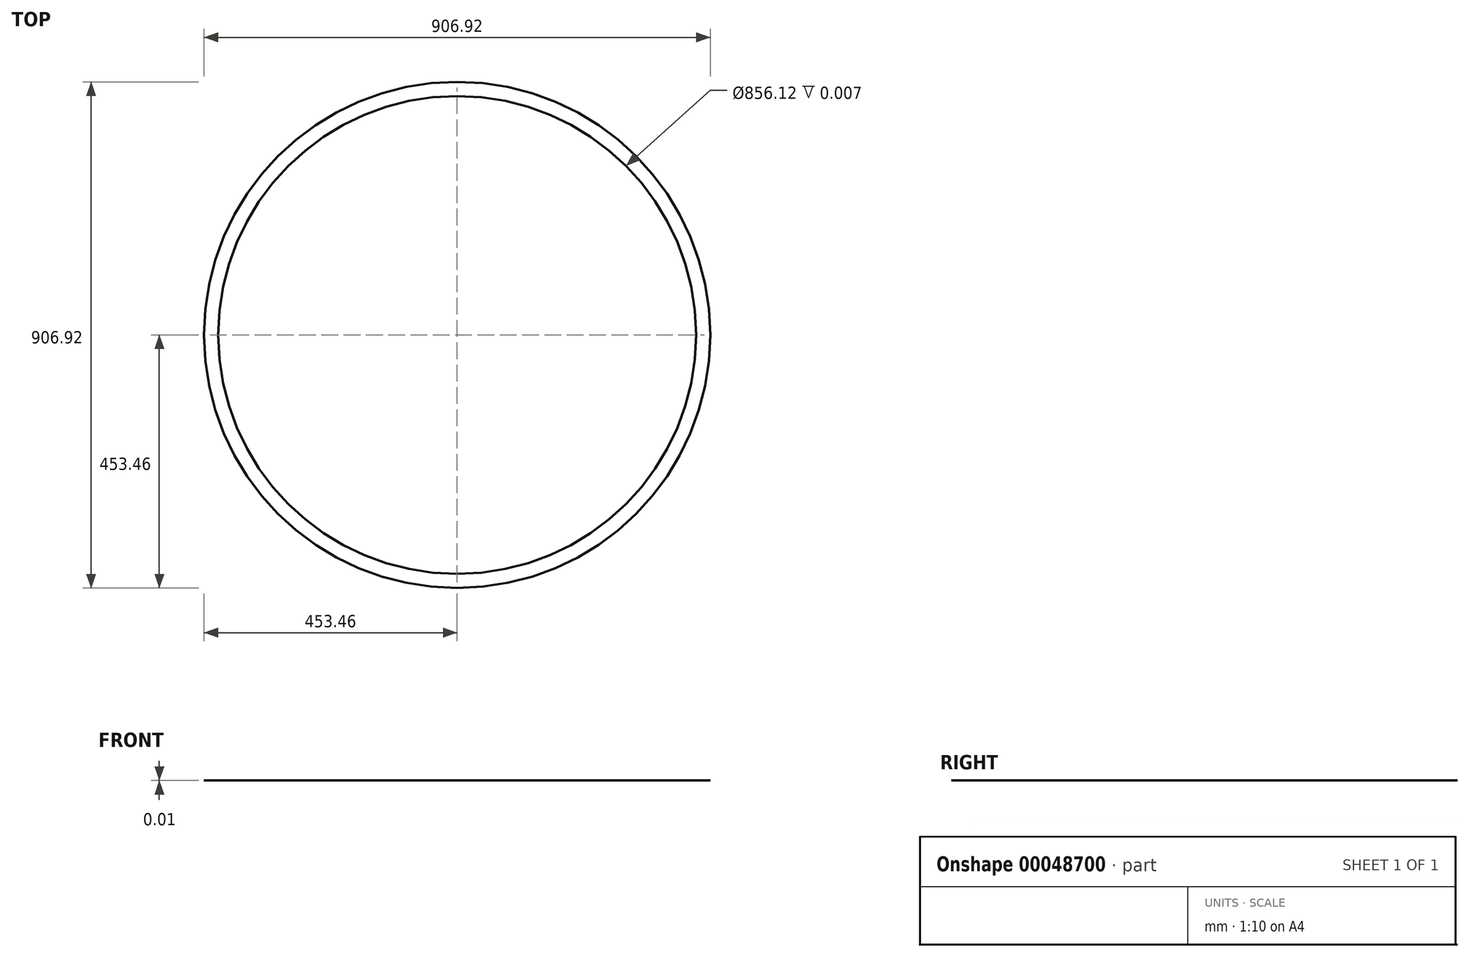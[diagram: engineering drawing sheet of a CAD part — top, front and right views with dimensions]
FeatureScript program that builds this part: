
annotation { "Feature Type Name" : "Feature", "Feature Type Description" : "" }
export const myFeature = defineFeature(function(context is Context, id is Id, definition is map)
    precondition{}
    {
        {
            var Q0;
            Q0=qCreatedBy(makeId("Top.planeOp"),FACE);
            var sketch = newSketch(context, id + "F0", { "sketchPlane" : qUnion([Q0])});
            skCircle(sketch, "E0", {"center": v(0, 0) * mm, "radius": 453.46 * mm});
            skCircle(sketch, "E1", {"center": v(0, 0) * mm, "radius": 428.06 * mm});
            skSolve(sketch);
        }
        {
            var Q0;
            Q0 = qSketchRegion(id + "F0", true);
            extrude(context, id + "F1", {"entities" : qUnion([Q0]), "depth" : 3 / 457.2 * mm});
        }
    });
